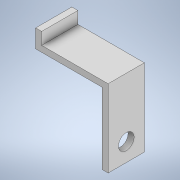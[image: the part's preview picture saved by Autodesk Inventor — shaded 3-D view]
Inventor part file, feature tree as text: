
AUTODESK INVENTOR PART (.ipt)
format: ipt  version: 2022 (Build 260153000, 153)  size: 122,880 bytes
history: native  units: mm
features: extrude x4, sketch x4
ambient origin geometry x8: Origin, YZ Plane, XZ Plane, XY Plane, X Axis, Y Axis, Z Axis, Center Point
bodies: Solid1 (feature_tree)
feature tree (8):
  extrude  "Extrusion1"  Depth=30.0mm
  extrude  "Extrusion2"  Depth=5.0mm
  extrude  "Extrusion3"  Depth=5.0mm
  extrude  "Extrusion4"  Depth=59.0mm
  sketch  "Sketch1"  dims[d0=60.0mm d1=30.0mm]
  sketch  "Sketch2"  dims[d2=5.0mm d3=0.0mm d4=5.0mm]
  sketch  "Sketch3"  dims[d5=10.0mm d6=0.0mm d7=5.0mm]
  sketch  "Sketch4"  dims[d8=59.0mm d9=0.0mm d11=13.0mm d12=59.0mm d13=0.0mm]
